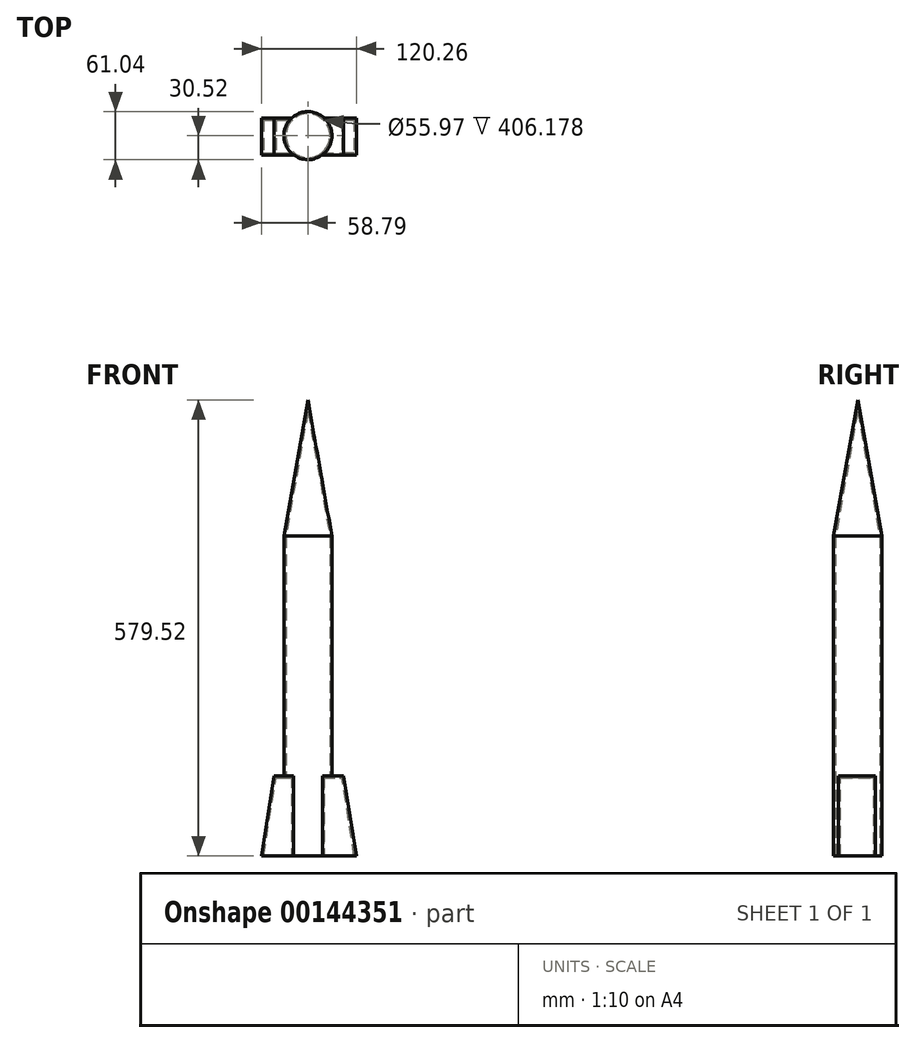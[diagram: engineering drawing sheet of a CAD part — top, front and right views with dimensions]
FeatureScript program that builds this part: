
annotation { "Feature Type Name" : "Feature", "Feature Type Description" : "" }
export const myFeature = defineFeature(function(context is Context, id is Id, definition is map)
    precondition{}
    {
        {
            var Q0;
            Q0=qCreatedBy(makeId("Top.planeOp"),FACE);
            var sketch = newSketch(context, id + "F0", { "sketchPlane" : qUnion([Q0])});
            skCircle(sketch, "E0", {"center": v(0, 0) * mm, "radius": 30.52 * mm});
            skSolve(sketch);
        }
        {
            var Q0;
            Q0 = qSketchRegion(id + "F0", true);
            extrude(context, id + "F1", {"entities" : qUnion([Q0]), "depth" : 406.4 * mm});
        }
        {
            var Q0;
            Q0=makeQuery(id+"F1.opExtrude","CAP_FACE",FACE,{"disambiguationData":[OSD([sQuery(id+"F0.wireOp",EDGE,"E0")])],"isStart":false});
            extrude(context, id + "F2", {"entities" : qUnion([Q0]), "operationType" : NewBodyOperationType.ADD, "depth" : 508 * mm, "hasDraft" : true, "draftAngle" : 10 * degree, "draftPullDirection" : true});
        }
        {
            var Q0;
            Q0=qCreatedBy(makeId("Top.planeOp"),FACE);
            var sketch = newSketch(context, id + "F3", { "sketchPlane" : qUnion([Q0])});
            skLineSegment(sketch, "E1.bottom", {"start": v(-61.15, -24.44) * mm, "end": v(71.29, -24.44) * mm});
            skLineSegment(sketch, "E1.top", {"start": v(-61.15, 22.41) * mm, "end": v(71.29, 22.41) * mm});
            skLineSegment(sketch, "E1.left", {"start": v(-61.15, -24.44) * mm, "end": v(-61.15, 22.41) * mm});
            skLineSegment(sketch, "E1.right", {"start": v(71.29, -24.44) * mm, "end": v(71.29, 22.41) * mm});
            skSolve(sketch);
        }
        {
            var Q0;
            Q0=makeQuery(id+"F3.imprint","IMPRINT",FACE,{"disambiguationData":[TD([[makeQuery(id+"F3.imprint","IMPRINT",EDGE,{"derivedFrom":sQuery(id+"F3.wireOp",EDGE,"E1.bottom")}),1.0]])]});
            extrude(context, id + "F4", {"entities" : qUnion([Q0]), "operationType" : NewBodyOperationType.ADD, "depth" : 101.6 * mm});
        }
        {
            var Q0;
            Q0=qCreatedBy(makeId("Front.planeOp"),FACE);
            var sketch = newSketch(context, id + "F5", { "sketchPlane" : qUnion([Q0])});
            skLineSegment(sketch, "E2", {"start": v(43.18, 115.92) * mm, "end": v(67.67, -39.33) * mm});
            skLineSegment(sketch, "E3", {"start": v(67.67, -39.33) * mm, "end": v(111.75, 92.9) * mm});
            skLineSegment(sketch, "E4", {"start": v(111.75, 92.9) * mm, "end": v(43.18, 115.92) * mm});
            skLineSegment(sketch, "E5", {"start": v(-41.05, 113.47) * mm, "end": v(-69.46, -68.23) * mm});
            skLineSegment(sketch, "E6", {"start": v(-69.46, -68.23) * mm, "end": v(-116.47, -18.76) * mm});
            skLineSegment(sketch, "E7", {"start": v(-116.47, -18.76) * mm, "end": v(-71.9, 117.88) * mm});
            skLineSegment(sketch, "E8", {"start": v(-71.9, 117.88) * mm, "end": v(-41.05, 113.47) * mm});
            skSolve(sketch);
        }
        {
            var Q0;
            Q0 = qSketchRegion(id + "F5", true);
            extrude(context, id + "F6", {"entities" : qUnion([Q0]), "operationType" : NewBodyOperationType.REMOVE, "endBound" : BoundingType.SYMMETRIC, "oppositeDirection" : true, "depth" : 1383.77 * mm});
        }
        {
            var Q0;
            Q0=makeQuery(id+"F4.boolean.opBoolean","MERGE",FACE,{"derivedFrom":[makeQuery(id+"F1.opExtrude","CAP_FACE",FACE,{"disambiguationData":[OSD([sQuery(id+"F0.wireOp",EDGE,"E0")])],"isStart":true}),makeQuery(id+"F4.opExtrude","CAP_FACE",FACE,{"disambiguationData":[OSD([sQuery(id+"F3.wireOp",EDGE,"E1.bottom"),sQuery(id+"F3.wireOp",EDGE,"E1.top"),sQuery(id+"F3.wireOp",EDGE,"E1.left"),sQuery(id+"F3.wireOp",EDGE,"E1.right")])],"isStart":true})]});
            shell(context, id + "F7", {"entities" : qUnion([Q0]), "thickness" : 2.54 * mm});
        }
    });
